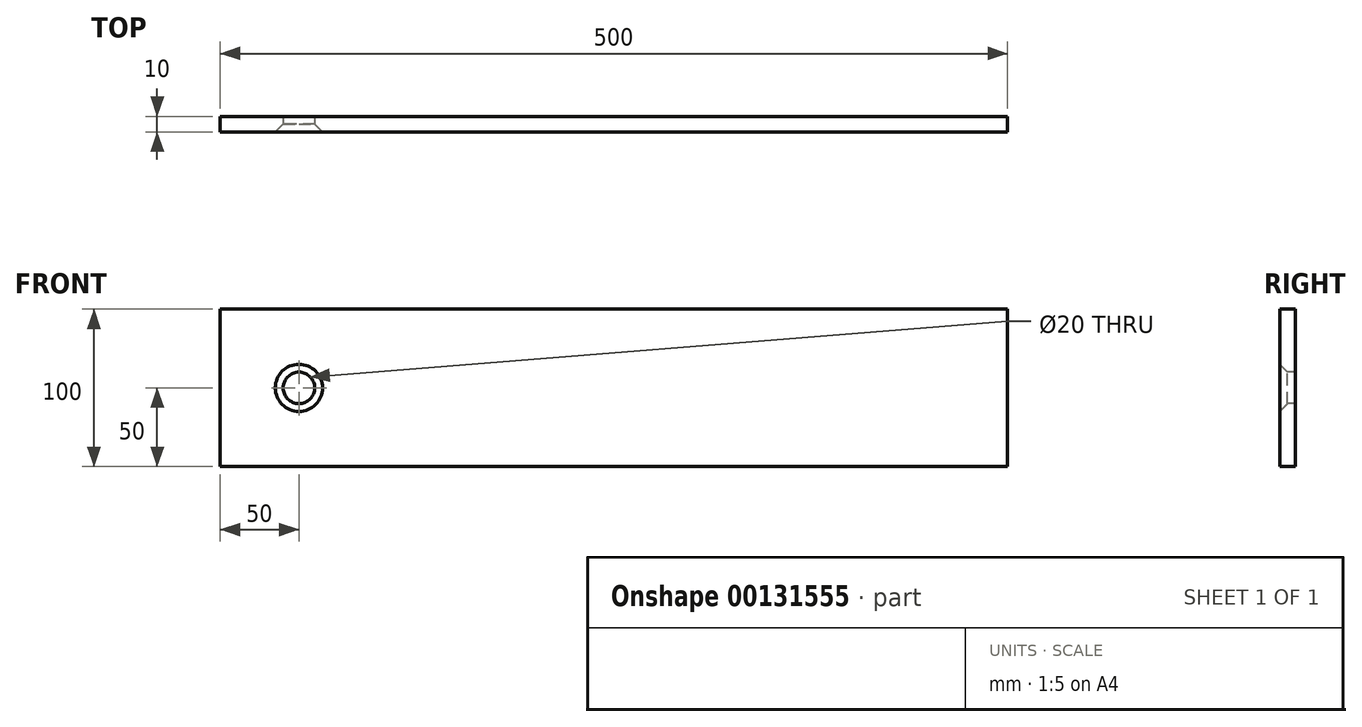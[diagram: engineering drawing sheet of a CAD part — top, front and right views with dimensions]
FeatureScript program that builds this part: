
annotation { "Feature Type Name" : "Feature", "Feature Type Description" : "" }
export const myFeature = defineFeature(function(context is Context, id is Id, definition is map)
    precondition{}
    {
        {
            var Q0;
            Q0=qCreatedBy(makeId("Right.planeOp"),FACE);
            var sketch = newSketch(context, id + "F0", { "sketchPlane" : qUnion([Q0])});
            skLineSegment(sketch, "E0.bottom", {"start": v(5, 50) * mm, "end": v(-5, 50) * mm});
            skLineSegment(sketch, "E0.top", {"start": v(5, -50) * mm, "end": v(-5, -50) * mm});
            skLineSegment(sketch, "E0.left", {"start": v(5, 50) * mm, "end": v(5, -50) * mm});
            skLineSegment(sketch, "E0.right", {"start": v(-5, 50) * mm, "end": v(-5, -50) * mm});
            skPoint(sketch, "E0.middle", {"position": v(0, 0) * mm});
            skSolve(sketch);
        }
        {
            var Q0;
            Q0=makeQuery(id+"F0.imprint","IMPRINT",FACE,{"disambiguationData":[TD([[makeQuery(id+"F0.imprint","IMPRINT",EDGE,{"derivedFrom":sQuery(id+"F0.wireOp",EDGE,"E0.bottom")}),1.0]])]});
            extrude(context, id + "F1", {"entities" : qUnion([Q0]), "depth" : 500 * mm, "symmetric" : true});
        }
        {
            var Q0;
            Q0=makeQuery(id+"F1.opExtrude","SWEPT_FACE",FACE,{"disambiguationData":[OSD([sQuery(id+"F0.wireOp",EDGE,"E0.right")])]});
            var sketch = newSketch(context, id + "F2", { "sketchPlane" : qUnion([Q0])});
            skPoint(sketch, "E1", {"position": v(-200, 0) * mm});
            skSolve(sketch);
        }
        {
            var Q0;
            Q0=sQuery(id+"F2.wireOp",VERTEX,"E1");
            var Q1;
            Q1=makeQuery(id+"F1.opExtrude","SWEPT_BODY",BODY,{"disambiguationData":[OSD([sQuery(id+"F0.wireOp",EDGE,"E0.bottom"),sQuery(id+"F0.wireOp",EDGE,"E0.top"),sQuery(id+"F0.wireOp",EDGE,"E0.left"),sQuery(id+"F0.wireOp",EDGE,"E0.right")])]});
            hole(context, id + "F3", {"style" : HoleStyle.C_SINK, "endStyle" : HoleEndStyle.THROUGH, "holeDiameter" : 20 * mm, "cSinkDiameter" : 30 * mm, "cSinkAngle" : 90 * degree, "locations" : qUnion([Q0]), "scope" : qUnion([Q1]), "isTappedThrough" : true});
        }
    });
